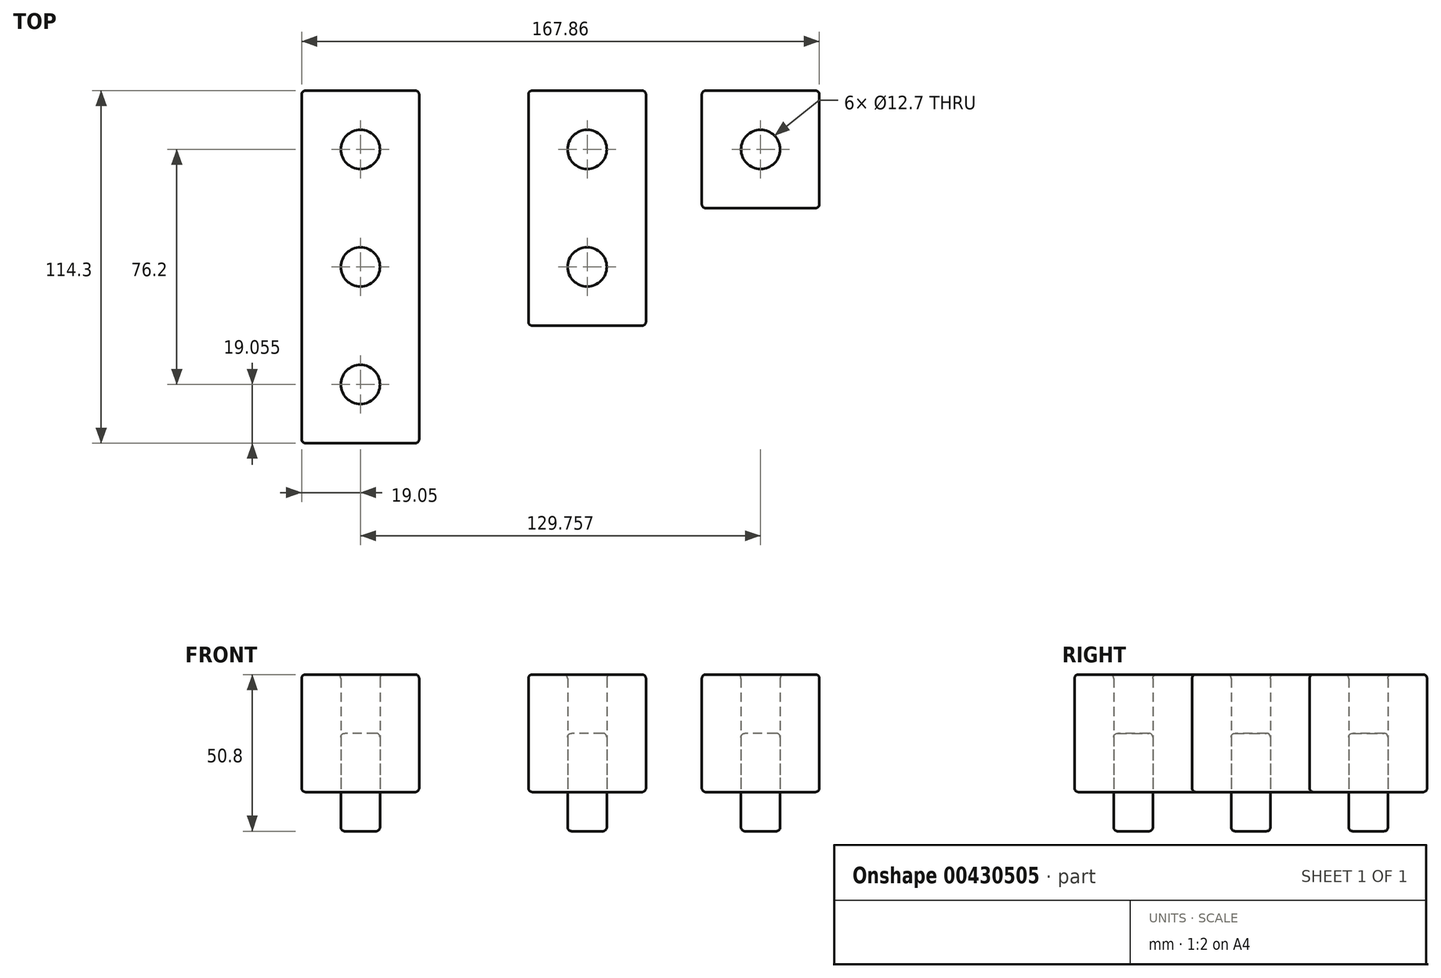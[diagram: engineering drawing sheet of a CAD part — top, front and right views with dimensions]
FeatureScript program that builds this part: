
annotation { "Feature Type Name" : "Feature", "Feature Type Description" : "" }
export const myFeature = defineFeature(function(context is Context, id is Id, definition is map)
    precondition{}
    {
        {
            var Q0;
            Q0=qCreatedBy(makeId("Top.planeOp"),FACE);
            var sketch = newSketch(context, id + "F0", { "sketchPlane" : qUnion([Q0])});
            skLineSegment(sketch, "E0.bottom", {"start": v(-38.1, 79.37) * mm, "end": v(0, 79.37) * mm});
            skLineSegment(sketch, "E0.top", {"start": v(-38.1, -34.93) * mm, "end": v(0, -34.93) * mm});
            skLineSegment(sketch, "E0.left", {"start": v(-38.1, 79.37) * mm, "end": v(-38.1, -34.93) * mm});
            skLineSegment(sketch, "E0.right", {"start": v(0, 79.37) * mm, "end": v(0, -34.93) * mm});
            skCircle(sketch, "E1", {"center": v(-19.05, 60.32) * mm, "radius": 6.35 * mm});
            skPoint(sketch, "E1.centerSnap0", {"position": v(-19.05, 79.37) * mm});
            skCircle(sketch, "E2", {"center": v(-19.05, -15.88) * mm, "radius": 6.35 * mm});
            skPoint(sketch, "E2.centerSnap0", {"position": v(-19.05, -34.93) * mm});
            skCircle(sketch, "E3", {"center": v(-19.05, 22.22) * mm, "radius": 6.35 * mm});
            skLineSegment(sketch, "E4.bottom", {"start": v(35.42, 79.37) * mm, "end": v(73.52, 79.37) * mm});
            skLineSegment(sketch, "E4.top", {"start": v(35.42, 3.17) * mm, "end": v(73.52, 3.17) * mm});
            skLineSegment(sketch, "E4.left", {"start": v(35.42, 79.37) * mm, "end": v(35.42, 3.17) * mm});
            skLineSegment(sketch, "E4.right", {"start": v(73.52, 79.37) * mm, "end": v(73.52, 3.17) * mm});
            skLineSegment(sketch, "E5.bottom", {"start": v(91.66, 79.37) * mm, "end": v(129.76, 79.37) * mm});
            skLineSegment(sketch, "E5.top", {"start": v(91.66, 41.27) * mm, "end": v(129.76, 41.27) * mm});
            skLineSegment(sketch, "E5.left", {"start": v(91.66, 79.37) * mm, "end": v(91.66, 41.27) * mm});
            skLineSegment(sketch, "E5.right", {"start": v(129.76, 79.37) * mm, "end": v(129.76, 41.27) * mm});
            skCircle(sketch, "E6", {"center": v(54.47, 60.32) * mm, "radius": 6.35 * mm});
            skPoint(sketch, "E6.centerSnap0", {"position": v(54.47, 79.37) * mm});
            skCircle(sketch, "E7", {"center": v(54.47, 22.22) * mm, "radius": 6.35 * mm});
            skCircle(sketch, "E8", {"center": v(110.7, 60.32) * mm, "radius": 6.35 * mm});
            skPoint(sketch, "E8.centerSnap0", {"position": v(110.7, 79.37) * mm});
            skSolve(sketch);
        }
        {
            var Q0;
            Q0=makeQuery(id+"F0.imprint","IMPRINT",FACE,{"disambiguationData":[TD([[makeQuery(id+"F0.imprint","IMPRINT",EDGE,{"derivedFrom":sQuery(id+"F0.wireOp",EDGE,"E0.bottom")}),-1.0]])]});
            extrude(context, id + "F1", {"entities" : qUnion([Q0]), "depth" : 38.1 * mm});
        }
        {
            var Q0;
            Q0=makeQuery(id+"F0.imprint","IMPRINT",FACE,{"disambiguationData":[TD([[makeQuery(id+"F0.imprint","IMPRINT",EDGE,{"derivedFrom":sQuery(id+"F0.wireOp",EDGE,"E4.bottom")}),-1.0]])]});
            extrude(context, id + "F2", {"entities" : qUnion([Q0]), "depth" : 38.1 * mm});
        }
        {
            var Q0;
            Q0=makeQuery(id+"F0.imprint","IMPRINT",FACE,{"disambiguationData":[TD([[makeQuery(id+"F0.imprint","IMPRINT",EDGE,{"derivedFrom":sQuery(id+"F0.wireOp",EDGE,"E5.bottom")}),-1.0]])]});
            extrude(context, id + "F3", {"entities" : qUnion([Q0]), "depth" : 38.1 * mm});
        }
        {
            var Q0;
            Q0=makeQuery(id+"F0.imprint","IMPRINT",FACE,{"disambiguationData":[TD([[makeQuery(id+"F0.imprint","IMPRINT",EDGE,{"derivedFrom":sQuery(id+"F0.wireOp",EDGE,"E1")}),1.0]])]});
            var Q1;
            Q1=makeQuery(id+"F0.imprint","IMPRINT",FACE,{"disambiguationData":[TD([[makeQuery(id+"F0.imprint","IMPRINT",EDGE,{"derivedFrom":sQuery(id+"F0.wireOp",EDGE,"E3")}),1.0]])]});
            var Q2;
            Q2=makeQuery(id+"F0.imprint","IMPRINT",FACE,{"disambiguationData":[TD([[makeQuery(id+"F0.imprint","IMPRINT",EDGE,{"derivedFrom":sQuery(id+"F0.wireOp",EDGE,"E2")}),1.0]])]});
            var Q3;
            Q3=makeQuery(id+"F0.imprint","IMPRINT",FACE,{"disambiguationData":[TD([[makeQuery(id+"F0.imprint","IMPRINT",EDGE,{"derivedFrom":sQuery(id+"F0.wireOp",EDGE,"E7")}),1.0]])]});
            var Q4;
            Q4=makeQuery(id+"F0.imprint","IMPRINT",FACE,{"disambiguationData":[TD([[makeQuery(id+"F0.imprint","IMPRINT",EDGE,{"derivedFrom":sQuery(id+"F0.wireOp",EDGE,"E6")}),1.0]])]});
            var Q5;
            Q5=makeQuery(id+"F0.imprint","IMPRINT",FACE,{"disambiguationData":[TD([[makeQuery(id+"F0.imprint","IMPRINT",EDGE,{"derivedFrom":sQuery(id+"F0.wireOp",EDGE,"E8")}),1.0]])]});
            extrude(context, id + "F4", {"entities" : qUnion([Q0, Q1, Q2, Q3, Q4, Q5]), "depth" : 19.05 * mm, "hasSecondDirection" : true, "secondDirectionOppositeDirection" : true, "secondDirectionDepth" : 12.7 * mm});
        }
        {
            var Q0;
            Q0=makeQuery(id+"F1.opExtrude","SWEPT_FACE",FACE,{"disambiguationData":[OSD([sQuery(id+"F0.wireOp",EDGE,"E0.bottom")])]});
            var Q1;
            Q1=makeQuery(id+"F2.opExtrude","SWEPT_FACE",FACE,{"disambiguationData":[OSD([sQuery(id+"F0.wireOp",EDGE,"E4.bottom")])]});
            var Q2;
            Q2=makeQuery(id+"F3.opExtrude","SWEPT_FACE",FACE,{"disambiguationData":[OSD([sQuery(id+"F0.wireOp",EDGE,"E5.bottom")])]});
            var Q3;
            Q3=makeQuery(id+"F1.opExtrude","SWEPT_FACE",FACE,{"disambiguationData":[OSD([sQuery(id+"F0.wireOp",EDGE,"E0.left")])]});
            var Q4;
            Q4=makeQuery(id+"F2.opExtrude","SWEPT_FACE",FACE,{"disambiguationData":[OSD([sQuery(id+"F0.wireOp",EDGE,"E4.left")])]});
            var Q5;
            Q5=makeQuery(id+"F3.opExtrude","SWEPT_FACE",FACE,{"disambiguationData":[OSD([sQuery(id+"F0.wireOp",EDGE,"E5.left")])]});
            var Q6;
            Q6=makeQuery(id+"F3.opExtrude","SWEPT_FACE",FACE,{"disambiguationData":[OSD([sQuery(id+"F0.wireOp",EDGE,"E5.right")])]});
            var Q7;
            Q7=makeQuery(id+"F3.opExtrude","SWEPT_FACE",FACE,{"disambiguationData":[OSD([sQuery(id+"F0.wireOp",EDGE,"E5.top")])]});
            var Q8;
            Q8=makeQuery(id+"F2.opExtrude","SWEPT_FACE",FACE,{"disambiguationData":[OSD([sQuery(id+"F0.wireOp",EDGE,"E4.right")])]});
            var Q9;
            Q9=makeQuery(id+"F2.opExtrude","SWEPT_FACE",FACE,{"disambiguationData":[OSD([sQuery(id+"F0.wireOp",EDGE,"E4.top")])]});
            var Q10;
            Q10=makeQuery(id+"F1.opExtrude","SWEPT_FACE",FACE,{"disambiguationData":[OSD([sQuery(id+"F0.wireOp",EDGE,"E0.right")])]});
            var Q11;
            Q11=makeQuery(id+"F1.opExtrude","SWEPT_FACE",FACE,{"disambiguationData":[OSD([sQuery(id+"F0.wireOp",EDGE,"E0.top")])]});
            var Q12;
            Q12=makeQuery(id+"F1.opExtrude","CAP_EDGE",EDGE,{"disambiguationData":[OSD([sQuery(id+"F0.wireOp",EDGE,"E2")])],"isStart":false});
            var Q13;
            Q13=makeQuery(id+"F1.opExtrude","CAP_EDGE",EDGE,{"disambiguationData":[OSD([sQuery(id+"F0.wireOp",EDGE,"E3")])],"isStart":false});
            var Q14;
            Q14=makeQuery(id+"F1.opExtrude","CAP_EDGE",EDGE,{"disambiguationData":[OSD([sQuery(id+"F0.wireOp",EDGE,"E1")])],"isStart":false});
            var Q15;
            Q15=makeQuery(id+"F2.opExtrude","CAP_EDGE",EDGE,{"disambiguationData":[OSD([sQuery(id+"F0.wireOp",EDGE,"E6")])],"isStart":false});
            var Q16;
            Q16=makeQuery(id+"F2.opExtrude","CAP_EDGE",EDGE,{"disambiguationData":[OSD([sQuery(id+"F0.wireOp",EDGE,"E7")])],"isStart":false});
            var Q17;
            Q17=makeQuery(id+"F3.opExtrude","CAP_EDGE",EDGE,{"disambiguationData":[OSD([sQuery(id+"F0.wireOp",EDGE,"E8")])],"isStart":false});
            var Q18;
            Q18=makeQuery(id+"F4.opExtrude","CAP_EDGE",EDGE,{"disambiguationData":[OSD([sQuery(id+"F0.wireOp",EDGE,"E8")])],"isStart":false});
            var Q19;
            Q19=makeQuery(id+"F4.opExtrude","CAP_EDGE",EDGE,{"disambiguationData":[OSD([sQuery(id+"F0.wireOp",EDGE,"E8")])],"isStart":true});
            var Q20;
            Q20=makeQuery(id+"F4.opExtrude","CAP_EDGE",EDGE,{"disambiguationData":[OSD([sQuery(id+"F0.wireOp",EDGE,"E6")])],"isStart":true});
            var Q21;
            Q21=makeQuery(id+"F4.opExtrude","CAP_EDGE",EDGE,{"disambiguationData":[OSD([sQuery(id+"F0.wireOp",EDGE,"E6")])],"isStart":false});
            var Q22;
            Q22=makeQuery(id+"F4.opExtrude","CAP_EDGE",EDGE,{"disambiguationData":[OSD([sQuery(id+"F0.wireOp",EDGE,"E7")])],"isStart":false});
            var Q23;
            Q23=makeQuery(id+"F4.opExtrude","CAP_EDGE",EDGE,{"disambiguationData":[OSD([sQuery(id+"F0.wireOp",EDGE,"E7")])],"isStart":true});
            var Q24;
            Q24=makeQuery(id+"F4.opExtrude","CAP_EDGE",EDGE,{"disambiguationData":[OSD([sQuery(id+"F0.wireOp",EDGE,"E1")])],"isStart":true});
            var Q25;
            Q25=makeQuery(id+"F4.opExtrude","CAP_EDGE",EDGE,{"disambiguationData":[OSD([sQuery(id+"F0.wireOp",EDGE,"E1")])],"isStart":false});
            var Q26;
            Q26=makeQuery(id+"F4.opExtrude","CAP_EDGE",EDGE,{"disambiguationData":[OSD([sQuery(id+"F0.wireOp",EDGE,"E3")])],"isStart":false});
            var Q27;
            Q27=makeQuery(id+"F4.opExtrude","CAP_EDGE",EDGE,{"disambiguationData":[OSD([sQuery(id+"F0.wireOp",EDGE,"E3")])],"isStart":true});
            var Q28;
            Q28=makeQuery(id+"F4.opExtrude","CAP_EDGE",EDGE,{"disambiguationData":[OSD([sQuery(id+"F0.wireOp",EDGE,"E2")])],"isStart":true});
            var Q29;
            Q29=makeQuery(id+"F4.opExtrude","CAP_EDGE",EDGE,{"disambiguationData":[OSD([sQuery(id+"F0.wireOp",EDGE,"E2")])],"isStart":false});
            fillet(context, id + "F5", {"entities" : qUnion([Q0, Q1, Q2, Q3, Q4, Q5, Q6, Q7, Q8, Q9, Q10, Q11, Q12, Q13, Q14, Q15, Q16, Q17, Q18, Q19, Q20, Q21, Q22, Q23, Q24, Q25, Q26, Q27, Q28, Q29]), "radius" : 1.27 * mm, "tangentPropagation" : true, "allowEdgeOverflow" : false});
        }
    });
